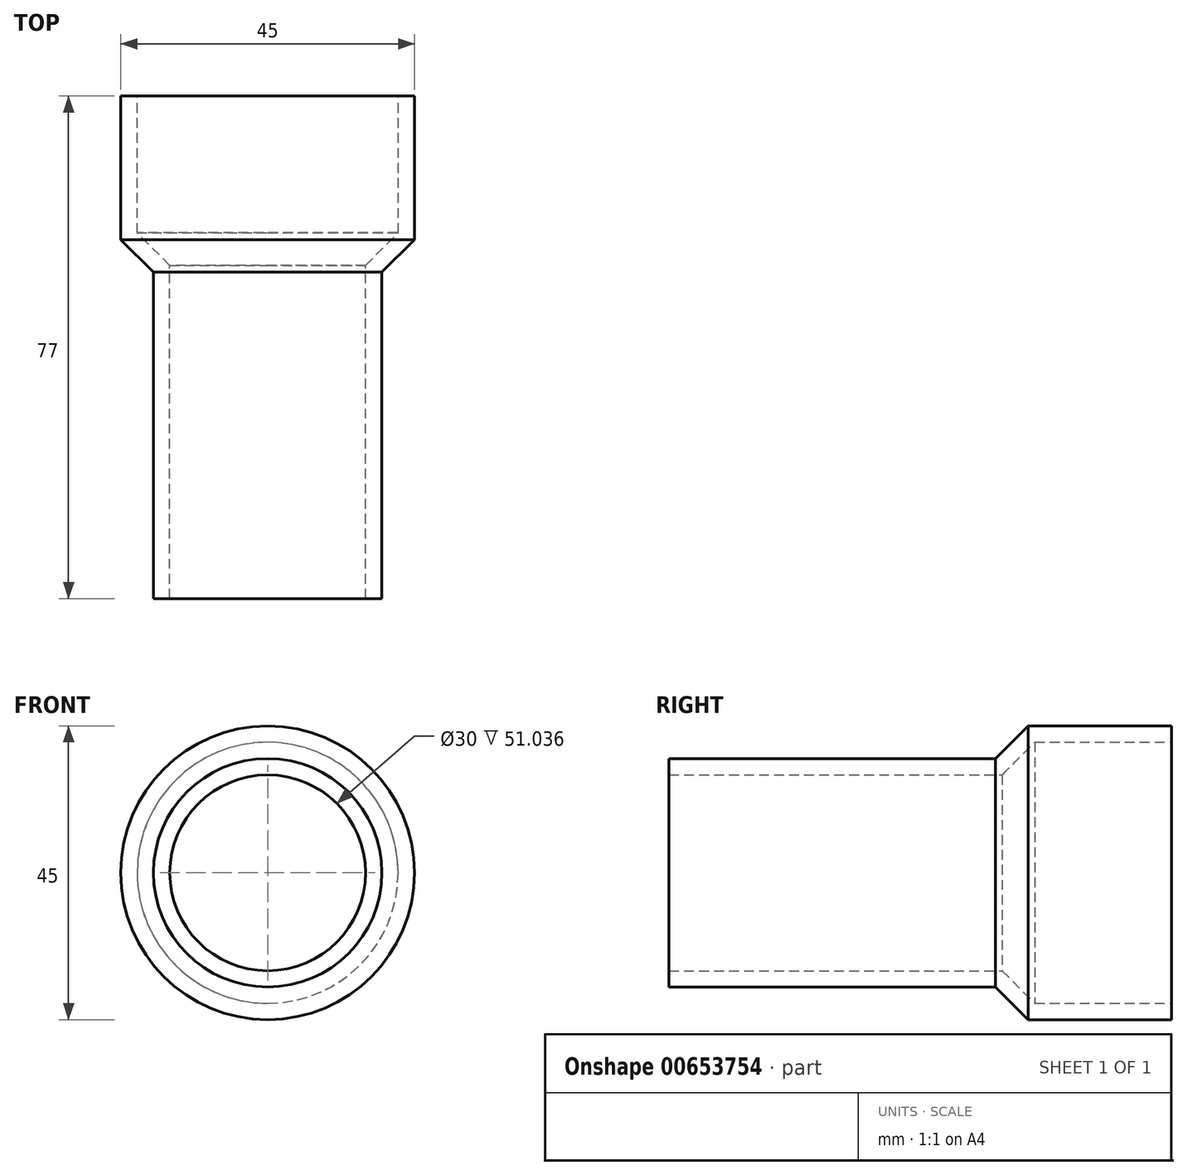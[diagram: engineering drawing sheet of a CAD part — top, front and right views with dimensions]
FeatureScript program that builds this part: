
annotation { "Feature Type Name" : "Feature", "Feature Type Description" : "" }
export const myFeature = defineFeature(function(context is Context, id is Id, definition is map)
    precondition{}
    {
        {
            var Q0;
            Q0=qCreatedBy(makeId("Front.planeOp"),FACE);
            var sketch = newSketch(context, id + "F0", { "sketchPlane" : qUnion([Q0])});
            skCircle(sketch, "E0", {"center": v(0, 0) * mm, "radius": 22.5 * mm});
            skSolve(sketch);
        }
        {
            var Q0;
            Q0 = qSketchRegion(id + "F0", true);
            extrude(context, id + "F1", {"entities" : qUnion([Q0]), "depth" : 27 * mm, "offsetDistance" : 25 * mm});
        }
        {
            var Q0;
            Q0=makeQuery(id+"F1.opExtrude","CAP_FACE",FACE,{"disambiguationData":[OSD([sQuery(id+"F0.wireOp",EDGE,"E0")])],"isStart":false});
            var sketch = newSketch(context, id + "F2", { "sketchPlane" : qUnion([Q0])});
            skCircle(sketch, "E1", {"center": v(0, 0) * mm, "radius": 17.5 * mm});
            skSolve(sketch);
        }
        {
            var Q0;
            Q0 = qSketchRegion(id + "F2", true);
            extrude(context, id + "F3", {"entities" : qUnion([Q0]), "operationType" : NewBodyOperationType.ADD, "depth" : 50 * mm, "offsetDistance" : 25 * mm});
        }
        {
            var Q0;
            Q0=makeQuery(id+"F1.opExtrude","CAP_EDGE",EDGE,{"disambiguationData":[OSD([sQuery(id+"F0.wireOp",EDGE,"E0")])],"isStart":false});
            chamfer(context, id + "F4", {"entities" : qUnion([Q0]), "width" : 5 * mm, "tangentPropagation" : true});
        }
        {
            var Q0;
            Q0=makeQuery(id+"F1.opExtrude","CAP_FACE",FACE,{"disambiguationData":[OSD([sQuery(id+"F0.wireOp",EDGE,"E0")])],"isStart":true});
            var Q1;
            Q1=makeQuery(id+"F3.opExtrude","CAP_FACE",FACE,{"disambiguationData":[OSD([sQuery(id+"F2.wireOp",EDGE,"E1")])],"isStart":false});
            shell(context, id + "F5", {"entities" : qUnion([Q0, Q1]), "thickness" : 2.5 * mm});
        }
    });
